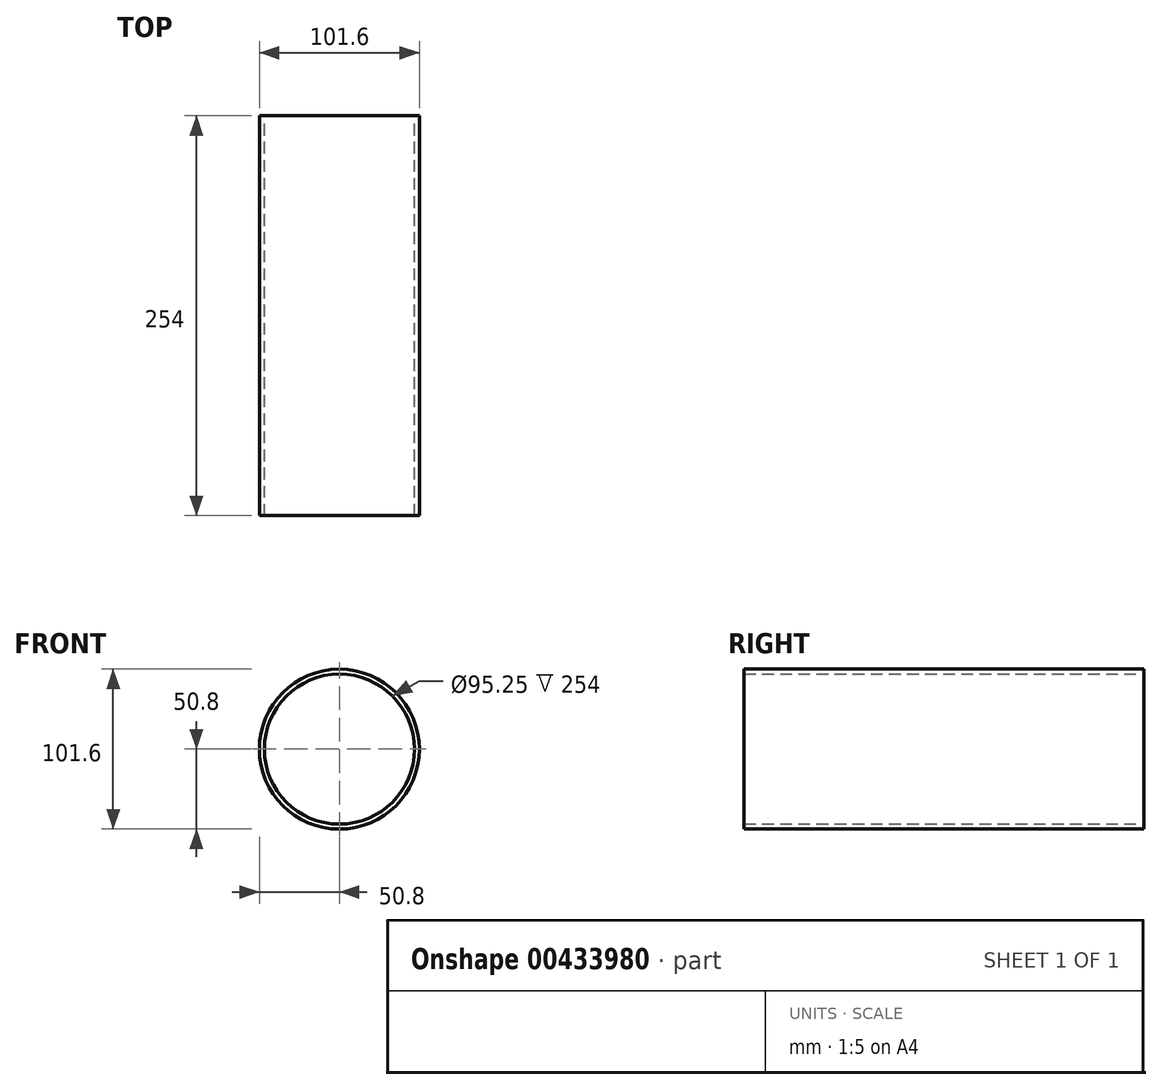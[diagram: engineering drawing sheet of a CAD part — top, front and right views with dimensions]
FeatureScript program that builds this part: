
annotation { "Feature Type Name" : "Feature", "Feature Type Description" : "" }
export const myFeature = defineFeature(function(context is Context, id is Id, definition is map)
    precondition{}
    {
        {
            var Q0;
            Q0=qCreatedBy(makeId("Front.planeOp"),FACE);
            var sketch = newSketch(context, id + "F0", { "sketchPlane" : qUnion([Q0])});
            skCircle(sketch, "E0", {"center": v(0, 0) * mm, "radius": 50.8 * mm});
            skCircle(sketch, "E1", {"center": v(0, 0) * mm, "radius": 47.63 * mm});
            skSolve(sketch);
        }
        {
            var Q0;
            Q0=makeQuery(id+"F0.imprint","IMPRINT",FACE,{"disambiguationData":[TD([[makeQuery(id+"F0.imprint","IMPRINT",EDGE,{"derivedFrom":sQuery(id+"F0.wireOp",EDGE,"E0")}),1.0]])]});
            extrude(context, id + "F1", {"entities" : qUnion([Q0]), "depth" : 254 * mm});
        }
    });
